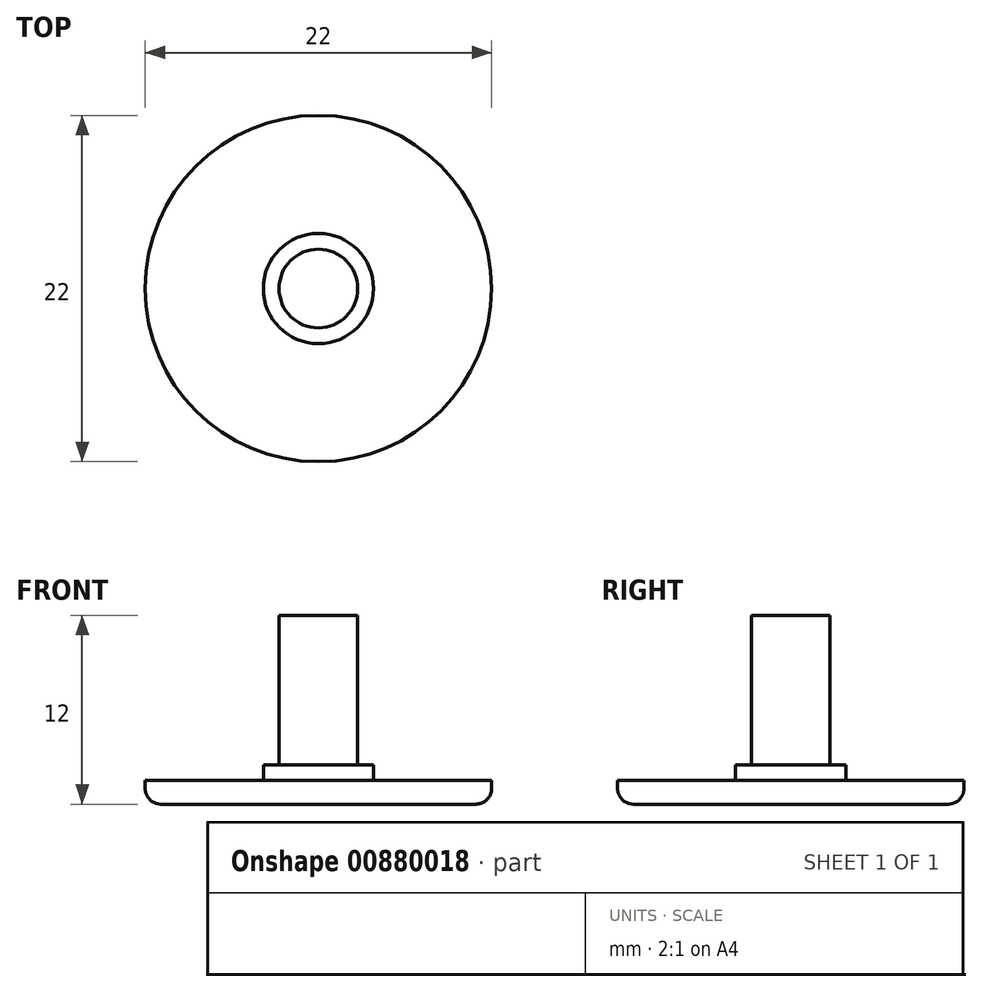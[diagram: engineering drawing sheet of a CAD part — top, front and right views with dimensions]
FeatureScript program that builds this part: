
annotation { "Feature Type Name" : "Feature", "Feature Type Description" : "" }
export const myFeature = defineFeature(function(context is Context, id is Id, definition is map)
    precondition{}
    {
        {
            var Q0;
            Q0=qCreatedBy(makeId("Top.planeOp"),FACE);
            var sketch = newSketch(context, id + "F0", { "sketchPlane" : qUnion([Q0])});
            skCircle(sketch, "E0", {"center": v(0, 0) * mm, "radius": 11 * mm});
            skSolve(sketch);
        }
        {
            var Q0;
            Q0 = qSketchRegion(id + "F0", true);
            extrude(context, id + "F1", {"entities" : qUnion([Q0]), "depth" : -1.5 * mm, "offsetDistance" : 25 * mm});
        }
        {
            var Q0;
            Q0=makeQuery(id+"F0.imprint","IMPRINT",FACE,{"disambiguationData":[TD([[makeQuery(id+"F0.imprint","IMPRINT",EDGE,{"derivedFrom":sQuery(id+"F0.wireOp",EDGE,"E0")}),1.0]])]});
            var sketch = newSketch(context, id + "F2", { "sketchPlane" : qUnion([Q0])});
            skCircle(sketch, "E1", {"center": v(0, 0) * mm, "radius": 3.5 * mm});
            skSolve(sketch);
        }
        {
            var Q0;
            Q0 = qSketchRegion(id + "F2", true);
            extrude(context, id + "F3", {"entities" : qUnion([Q0]), "operationType" : NewBodyOperationType.ADD, "depth" : 1 * mm, "offsetDistance" : 25 * mm});
        }
        {
            var Q0;
            Q0=makeQuery(id+"F3.opExtrude","CAP_FACE",FACE,{"disambiguationData":[OSD([sQuery(id+"F2.wireOp",EDGE,"E1")])],"isStart":false});
            var sketch = newSketch(context, id + "F4", { "sketchPlane" : qUnion([Q0])});
            skCircle(sketch, "E2", {"center": v(0, 0) * mm, "radius": 2.5 * mm});
            skSolve(sketch);
        }
        {
            var Q0;
            Q0 = qSketchRegion(id + "F4", true);
            extrude(context, id + "F5", {"entities" : qUnion([Q0]), "operationType" : NewBodyOperationType.ADD, "depth" : 9.5 * mm, "offsetDistance" : 25 * mm});
        }
        {
            var Q0;
            Q0=makeQuery(id+"F1.opExtrude","CAP_FACE",FACE,{"disambiguationData":[OSD([sQuery(id+"F0.wireOp",EDGE,"E0")])],"isStart":false});
            fillet(context, id + "F6", {"entities" : qUnion([Q0]), "radius" : 1 * mm, "tangentPropagation" : true, "allowEdgeOverflow" : false});
        }
    });
